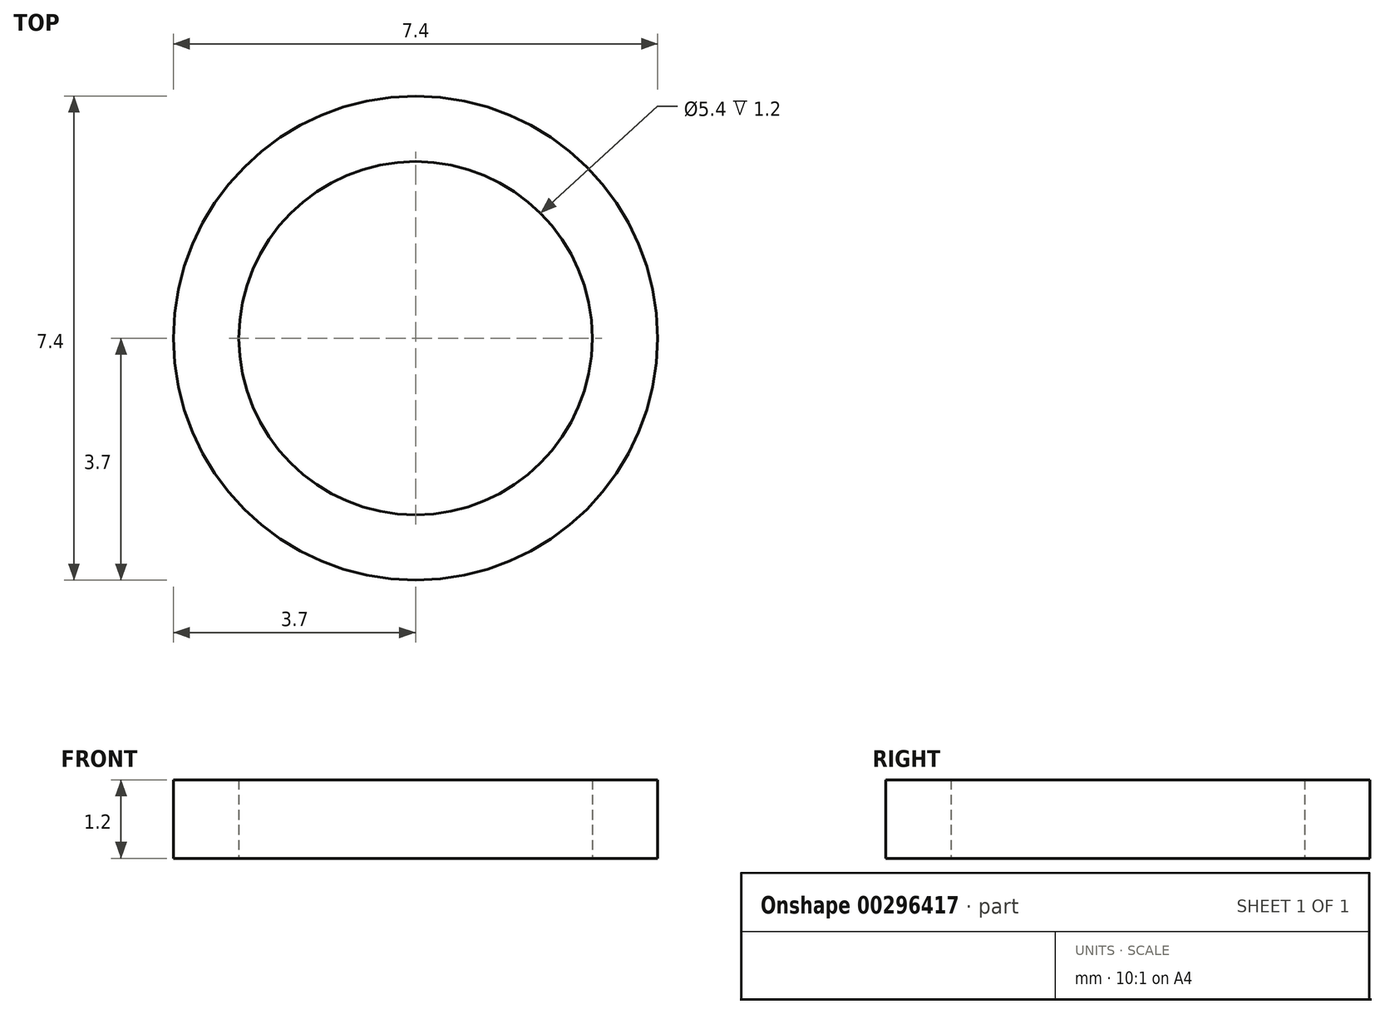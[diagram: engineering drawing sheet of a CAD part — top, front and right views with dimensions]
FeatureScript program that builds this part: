
annotation { "Feature Type Name" : "Feature", "Feature Type Description" : "" }
export const myFeature = defineFeature(function(context is Context, id is Id, definition is map)
    precondition{}
    {
        {
            var Q0;
            Q0=qCreatedBy(makeId("Top.planeOp"),FACE);
            var sketch = newSketch(context, id + "F0", { "sketchPlane" : qUnion([Q0])});
            skCircle(sketch, "E0", {"center": v(0, 0) * mm, "radius": 2.7 * mm});
            skCircle(sketch, "E1", {"center": v(0, 0) * mm, "radius": 3.7 * mm});
            skSolve(sketch);
        }
        {
            var Q0;
            Q0 = qSketchRegion(id + "F0", true);
            extrude(context, id + "F1", {"entities" : qUnion([Q0]), "depth" : 1.2 * mm, "offsetDistance" : 25 * mm});
        }
    });
